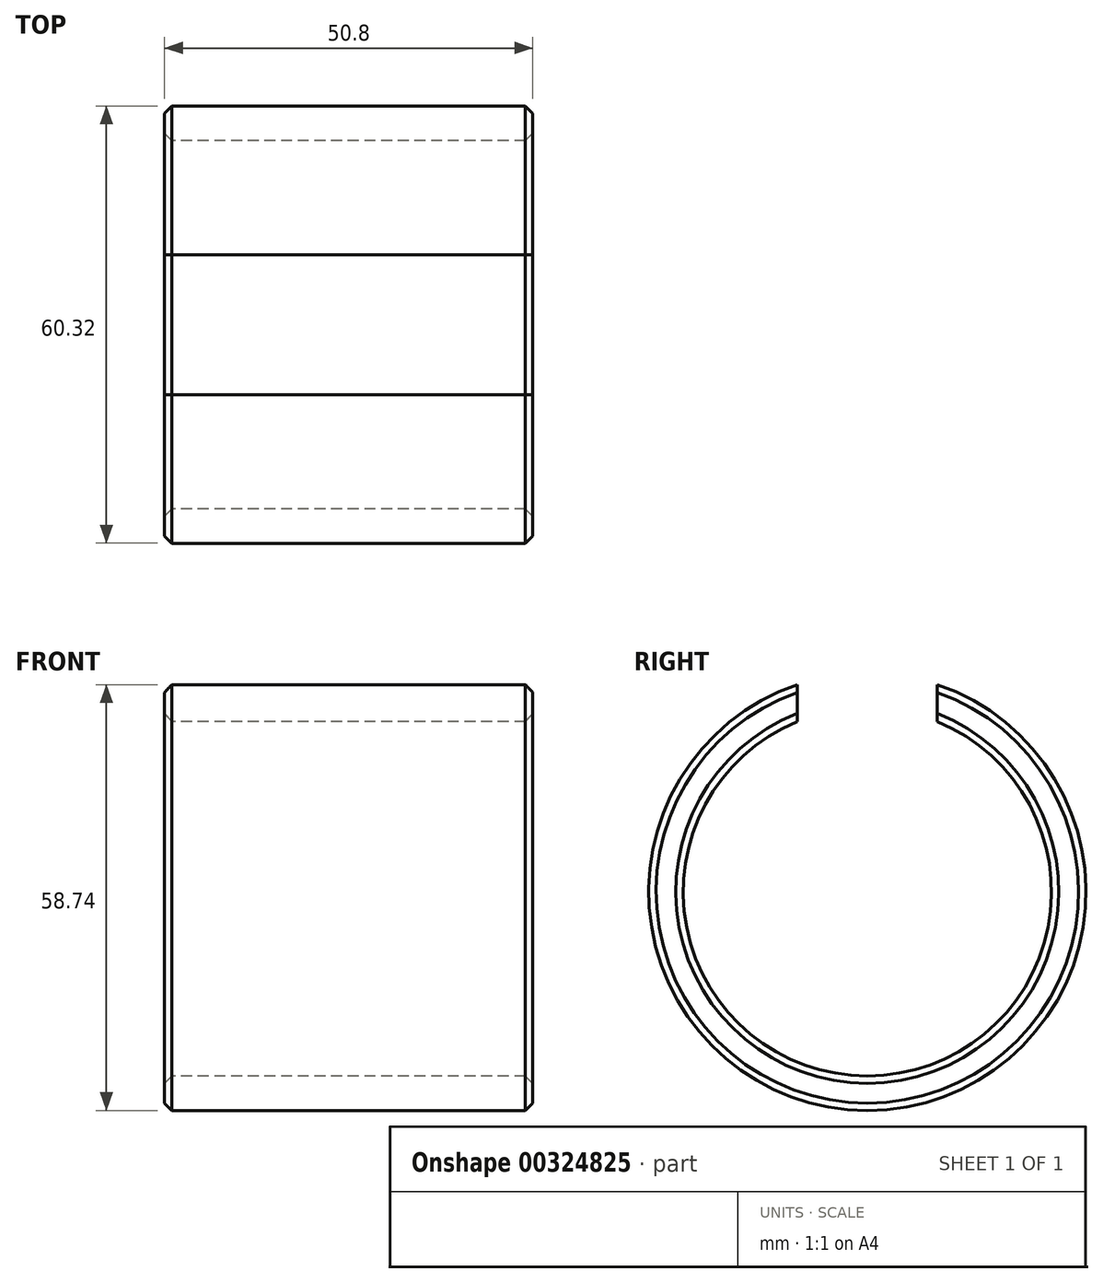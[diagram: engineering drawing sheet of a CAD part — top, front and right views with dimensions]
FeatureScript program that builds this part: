
annotation { "Feature Type Name" : "Feature", "Feature Type Description" : "" }
export const myFeature = defineFeature(function(context is Context, id is Id, definition is map)
    precondition{}
    {
        {
            var Q0;
            Q0=qCreatedBy(makeId("Right.planeOp"),FACE);
            var sketch = newSketch(context, id + "F0", { "sketchPlane" : qUnion([Q0])});
            skArc(sketch, "E0", {"start": v(-9.65, 28.58) * mm, "mid": v(0, -30.16) * mm, "end": v(9.65, 28.58) * mm});
            skArc(sketch, "E1", {"start": v(-9.65, 23.5) * mm, "mid": v(0, -25.4) * mm, "end": v(9.65, 23.5) * mm});
            skLineSegment(sketch, "E2", {"start": v(0, 0) * mm, "end": v(0, 44.25) * mm});
            skLineSegment(sketch, "E3.0", {"start": v(9.65, 0) * mm, "end": v(9.65, 44.25) * mm});
            skLineSegment(sketch, "E4.MirrorCS", {"start": v(-9.65, 0) * mm, "end": v(-9.65, 44.25) * mm});
            skSolve(sketch);
        }
        {
            var Q0;
            Q0=qSketchRegion(id+"F0",true);
            extrude(context, id + "F1", {"entities" : qUnion([Q0]), "endBound" : BoundingType.SYMMETRIC, "depth" : 50.8 * mm});
        }
        {
            var Q0;
            Q0=makeQuery(id+"F1.opExtrude","CAP_EDGE",EDGE,{"disambiguationData":[OSD([sQuery(id+"F0.wireOp",EDGE,"E0")])],"isStart":false});
            var Q1;
            Q1=makeQuery(id+"F1.opExtrude","CAP_EDGE",EDGE,{"disambiguationData":[OSD([sQuery(id+"F0.wireOp",EDGE,"E1")])],"isStart":false});
            var Q2;
            Q2=makeQuery(id+"F1.opExtrude","CAP_EDGE",EDGE,{"disambiguationData":[OSD([sQuery(id+"F0.wireOp",EDGE,"E0")])],"isStart":true});
            var Q3;
            Q3=makeQuery(id+"F1.opExtrude","CAP_EDGE",EDGE,{"disambiguationData":[OSD([sQuery(id+"F0.wireOp",EDGE,"E1")])],"isStart":true});
            chamfer(context, id + "F2", {"entities" : qUnion([Q0, Q1, Q2, Q3]), "width" : 1.02 * mm, "tangentPropagation" : true});
        }
    });
